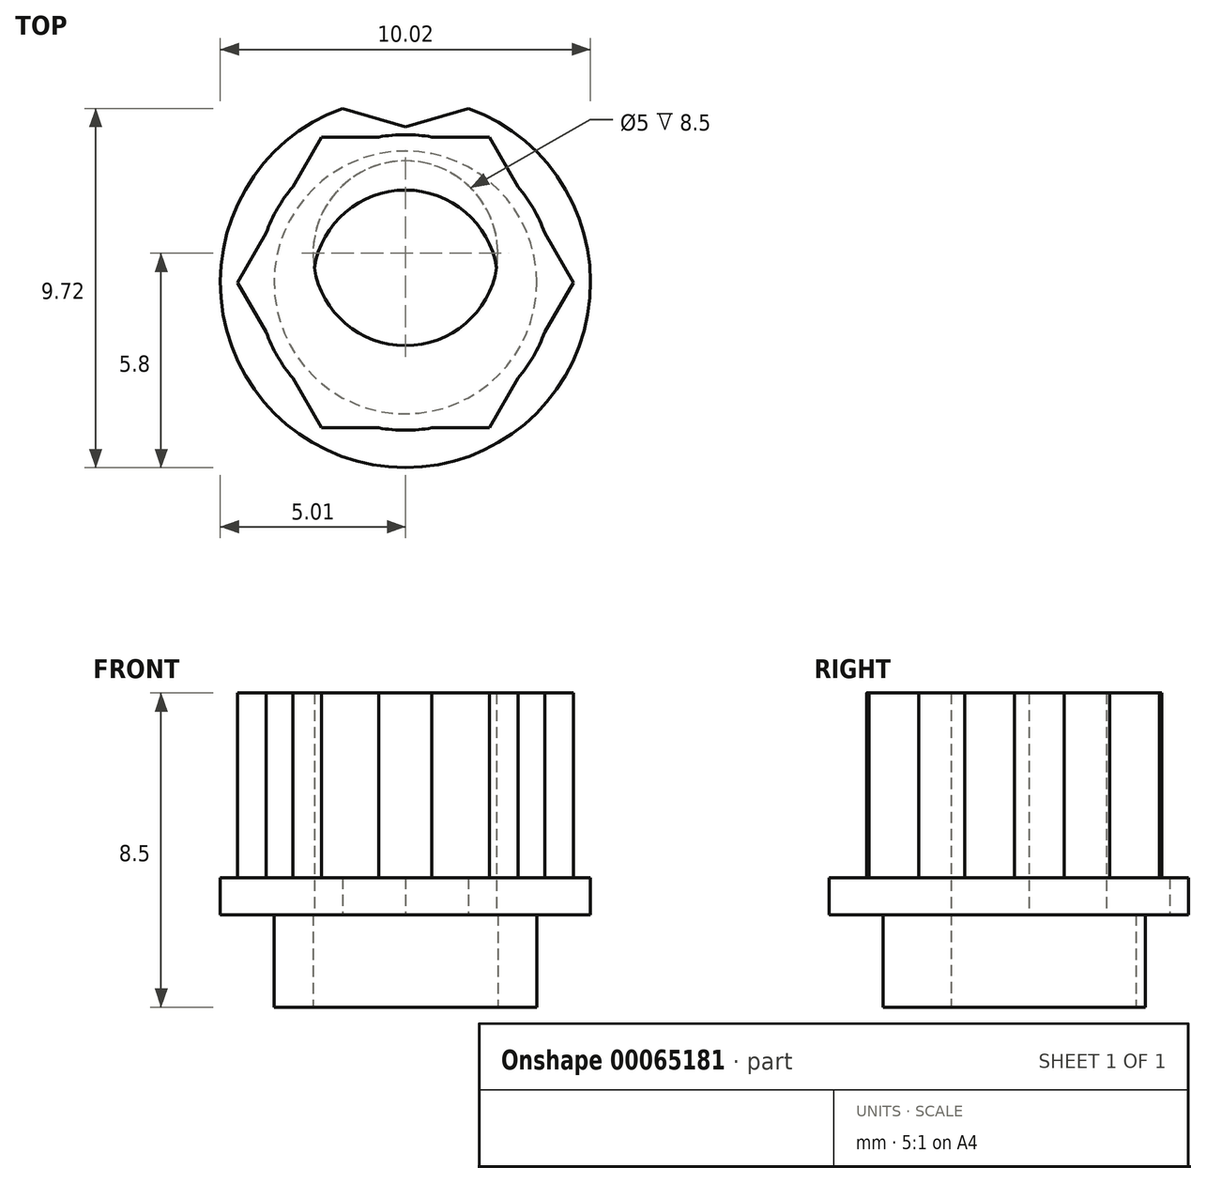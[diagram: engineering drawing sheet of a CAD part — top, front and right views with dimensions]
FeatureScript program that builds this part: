
annotation { "Feature Type Name" : "Feature", "Feature Type Description" : "" }
export const myFeature = defineFeature(function(context is Context, id is Id, definition is map)
    precondition{}
    {
        {
            var Q0;
            Q0=qCreatedBy(makeId("Top.planeOp"),FACE);
            var sketch = newSketch(context, id + "F0", { "sketchPlane" : qUnion([Q0])});
            skCircle(sketch, "E0", {"center": v(0, 0) * mm, "radius": 4 * mm});
            skCircle(sketch, "E1", {"center": v(0, 0) * mm, "radius": 2.5 * mm});
            skSolve(sketch);
        }
        {
            var Q0;
            Q0=makeQuery(id+"F0.imprint","IMPRINT",FACE,{"disambiguationData":[TD([[makeQuery(id+"F0.imprint","IMPRINT",EDGE,{"derivedFrom":sQuery(id+"F0.wireOp",EDGE,"E0")}),1.0]])]});
            extrude(context, id + "F1", {"entities" : qUnion([Q0]), "depth" : 1 * mm});
        }
        {
            var Q0;
            Q0=makeQuery(id+"F0.imprint","IMPRINT",FACE,{"disambiguationData":[TD([[makeQuery(id+"F0.imprint","IMPRINT",EDGE,{"derivedFrom":sQuery(id+"F0.wireOp",EDGE,"E0")}),1.0]])]});
            extrude(context, id + "F2", {"entities" : qUnion([Q0]), "depth" : 6 * mm});
        }
        {
            var Q0;
            Q0=qCreatedBy(makeId("Top.planeOp"),FACE);
            var sketch = newSketch(context, id + "F3", { "sketchPlane" : qUnion([Q0])});
            skArc(sketch, "E2", {"start": v(-1.7, 4.71) * mm, "mid": v(0, -5) * mm, "end": v(1.7, 4.71) * mm});
            skCircle(sketch, "E3", {"center": v(0, 0.79) * mm, "radius": 2.5 * mm});
            skCircle(sketch, "E4.cCircle", {"center": v(0, 0) * mm, "radius": 3.94 * mm, "construction": true});
            skLineSegment(sketch, "E4.0", {"start": v(2.27, -3.94) * mm, "end": v(-2.27, -3.94) * mm});
            skLineSegment(sketch, "E4.1", {"start": v(-2.27, -3.93) * mm, "end": v(-4.54, 0) * mm});
            skLineSegment(sketch, "E4.2", {"start": v(-4.54, 0) * mm, "end": v(-2.27, 3.93) * mm});
            skLineSegment(sketch, "E4.3", {"start": v(-2.27, 3.94) * mm, "end": v(2.27, 3.94) * mm});
            skLineSegment(sketch, "E4.4", {"start": v(2.27, 3.94) * mm, "end": v(4.54, 0) * mm});
            skLineSegment(sketch, "E4.5", {"start": v(4.54, 0) * mm, "end": v(2.27, -3.93) * mm});
            skPoint(sketch, "E4.0.midPoint", {"position": v(0, -3.94) * mm});
            skCircle(sketch, "E5", {"center": v(0, 0) * mm, "radius": 3.56 * mm});
            skLineSegment(sketch, "E6", {"start": v(-1.7, 4.71) * mm, "end": v(1.7, 4.71) * mm, "construction": true});
            skLineSegment(sketch, "E7", {"start": v(-1.7, 4.71) * mm, "end": v(0, 4.21) * mm});
            skLineSegment(sketch, "E8", {"start": v(0, 4.21) * mm, "end": v(1.7, 4.71) * mm});
            skPoint(sketch, "E9.end.orphan", {"position": v(0, 5.01) * mm});
            skSolve(sketch);
        }
        {
            var Q0;
            Q0=makeQuery(id+"F3.imprint","IMPRINT",FACE,{"disambiguationData":[TD([[makeQuery(id+"F3.imprint","IMPRINT",EDGE,{"derivedFrom":sQuery(id+"F3.wireOp",EDGE,"E4.0")}),-1.0]])]});
            var Q1;
            Q1=makeQuery(id+"F3.imprint","IMPRINT",FACE,{"disambiguationData":[TD([[makeQuery(id+"F3.imprint","IMPRINT",EDGE,{"derivedFrom":sQuery(id+"F3.wireOp",EDGE,"E3")}),-1.0]])]});
            extrude(context, id + "F4", {"entities" : qUnion([Q0, Q1]), "depth" : 6 * mm});
        }
        {
            var Q0;
            Q0=makeQuery(id+"F3.imprint","IMPRINT",FACE,{"disambiguationData":[TD([[makeQuery(id+"F3.imprint","IMPRINT",EDGE,{"derivedFrom":sQuery(id+"F3.wireOp",EDGE,"E2")}),1.0]])]});
            var Q1;
            Q1=sQuery(id+"F3.wireOp",EDGE,"E2");
            extrude(context, id + "F5", {"entities" : qUnion([Q0]), "operationType" : NewBodyOperationType.ADD, "surfaceEntities" : qUnion([Q1]), "depth" : 1 * mm});
        }
        {
            var Q0;
            Q0=makeQuery(id+"F3.imprint","IMPRINT",FACE,{"disambiguationData":[TD([[makeQuery(id+"F3.imprint","IMPRINT",EDGE,{"derivedFrom":sQuery(id+"F3.wireOp",EDGE,"E3")}),-1.0]])]});
            extrude(context, id + "F6", {"entities" : qUnion([Q0]), "operationType" : NewBodyOperationType.ADD, "oppositeDirection" : true, "depth" : 2.5 * mm});
        }
    });
